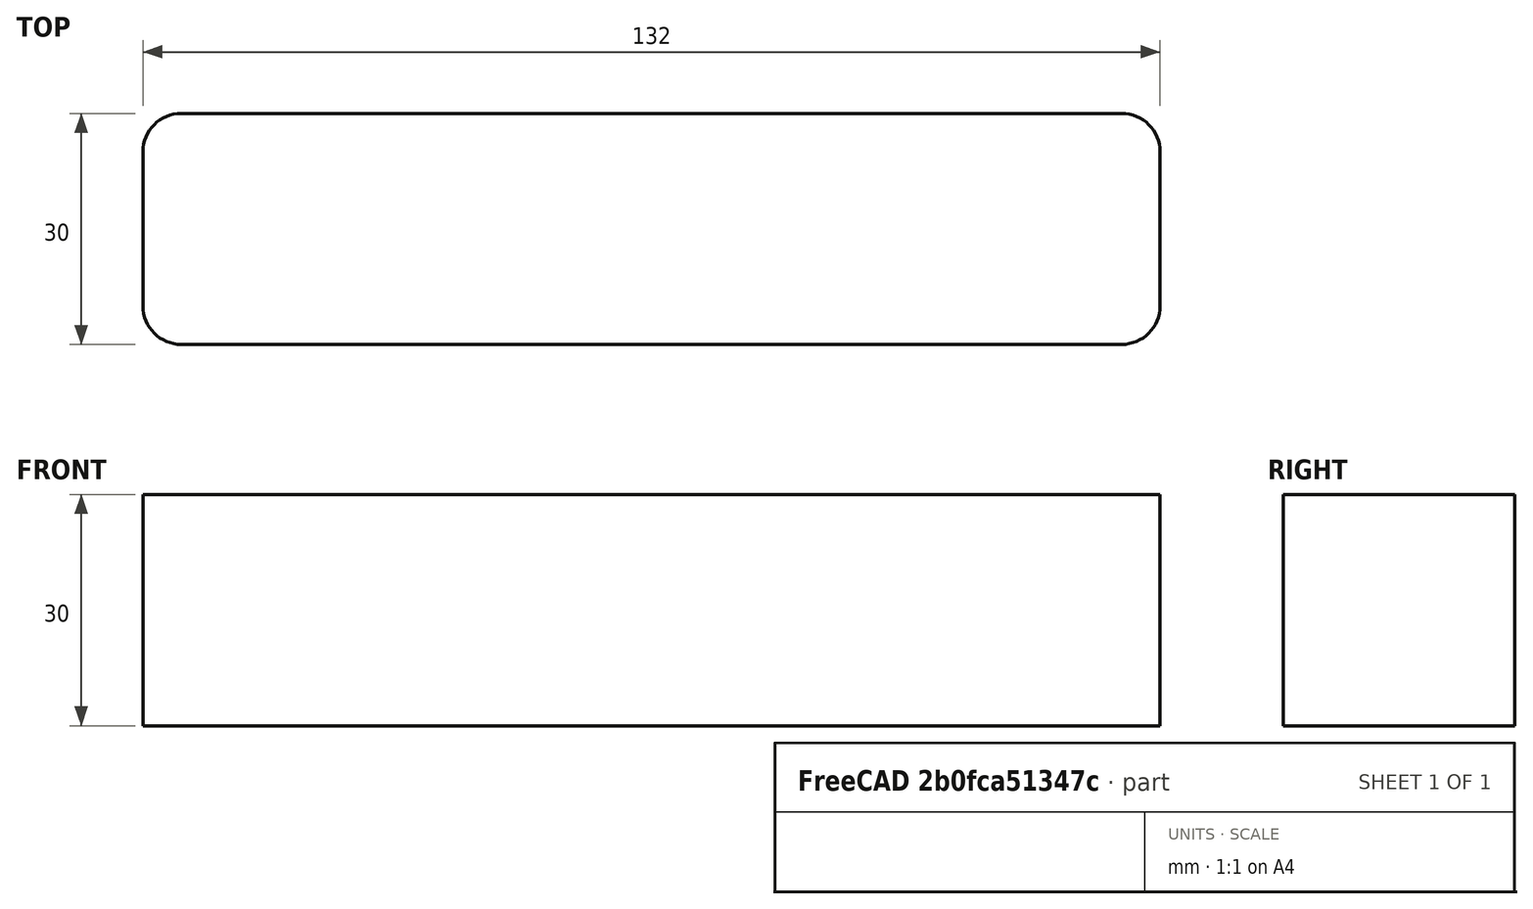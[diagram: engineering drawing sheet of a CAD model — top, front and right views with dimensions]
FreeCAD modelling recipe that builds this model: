
FCSTD DOCUMENT  (FreeCAD 0.18R4 (GitTag))
Label: v1
License: All rights reserved
LicenseURL: http://en.wikipedia.org/wiki/All_rights_reserved
objects: Sketcher::SketchObject×1, PartDesign::Pad×1, PartDesign::Body×1
note: 4 computed .brp shape members not serialized (recipe doc carries the construction recipe); baked Part::Feature solids carry a one-line shape summary decoded from their .brp

FEATURE [Sketcher::SketchObject] Sketch
  MapMode = 5
  Support = -> [XY_Plane]
  sketch-geometry (8):
    g0: LineSegment StartX=0 StartY=3.73e-14 StartZ=0 EndX=122 EndY=3.73e-14 EndZ=0
    g1: LineSegment StartX=127 StartY=5 StartZ=0 EndX=127 EndY=25 EndZ=0
    g2: LineSegment StartX=122 StartY=30 StartZ=0 EndX=0 EndY=30 EndZ=0
    g3: LineSegment StartX=-5 StartY=25 StartZ=0 EndX=-5 EndY=5 EndZ=0
    g4: ArcOfCircle CenterX=1.4e-15 CenterY=25 CenterZ=0 NormalX=0 NormalY=0 NormalZ=1 AngleXU=0 Radius=5 StartAngle=1.5708 EndAngle=3.14159
    g5: ArcOfCircle CenterX=1e-15 CenterY=5 CenterZ=0 NormalX=0 NormalY=0 NormalZ=1 AngleXU=0 Radius=5 StartAngle=3.14159 EndAngle=4.71239
    g6: ArcOfCircle CenterX=122 CenterY=5 CenterZ=0 NormalX=0 NormalY=0 NormalZ=1 AngleXU=0 Radius=5 StartAngle=4.71239 EndAngle=6.28319
    g7: ArcOfCircle CenterX=122 CenterY=25 CenterZ=0 NormalX=0 NormalY=0 NormalZ=1 AngleXU=0 Radius=5 StartAngle=1e-16 EndAngle=1.5708
  constraints (19):
    c: Horizontal(g0)
    c: Horizontal(g2)
    c: Vertical(g1)
    c: Vertical(g3)
    c: Tangent(g3,g4) = -1.5708
    c: Tangent(g2,g4) = -1.5708
    c: DistanceX(g3,g4) = 5
    c: Tangent(g3,g5) = -1.5708
    c: Tangent(g0,g5) = -1.5708
    c: Tangent(g0,g6) = -1.5708
    c: Tangent(g1,g6) = -1.5708
    c: Tangent(g2,g7) = -1.5708
    c: Tangent(g1,g7) = -1.5708
    c: DistanceX(g3,g5) = 5
    c: DistanceX(g6,g1) = 5
    c: DistanceX(g7,g1) = 5
    c: DistanceY(g0,g2) = 30
    c: DistanceX(g3,g1) = 132
    c: Coincident(g0,g-1)
FEATURE [PartDesign::Pad] Pad
  Length = 30
  Length2 = 100
  Profile = -> Sketch
  Type = 0
FEATURE [PartDesign::Body] Body
  Group = -> [Sketch,Pad]
  Origin = -> Origin
  Tip = -> Pad
